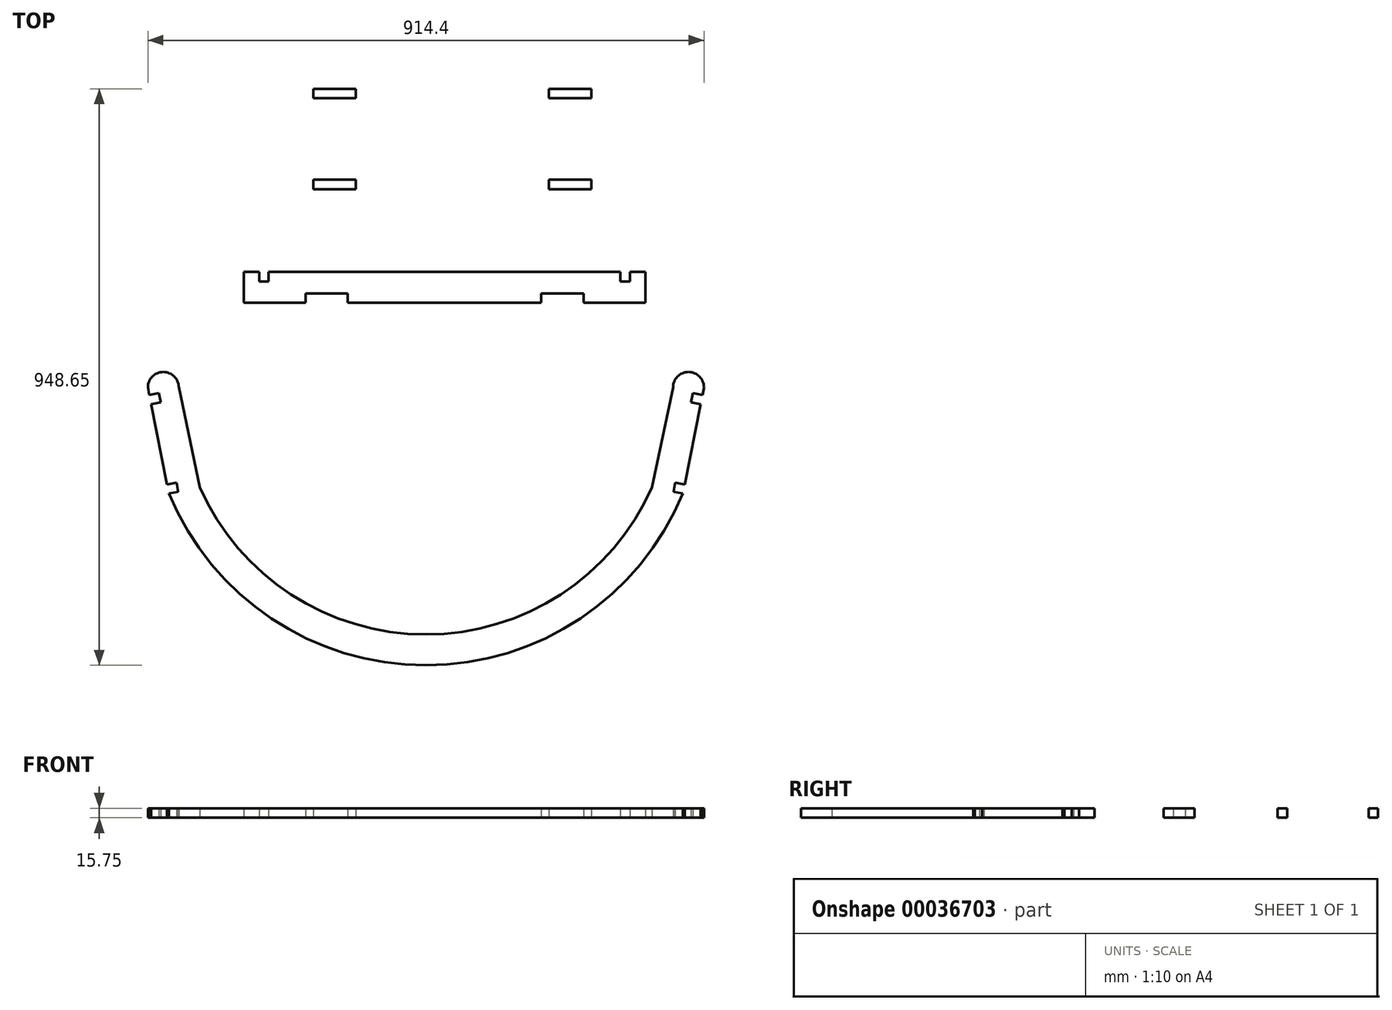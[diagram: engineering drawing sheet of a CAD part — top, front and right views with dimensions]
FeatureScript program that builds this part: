
annotation { "Feature Type Name" : "Feature", "Feature Type Description" : "" }
export const myFeature = defineFeature(function(context is Context, id is Id, definition is map)
    precondition{}
    {
        {
            var Q0;
            Q0=qCreatedBy(makeId("Top.planeOp"),FACE);
            var sketch = newSketch(context, id + "F0", { "sketchPlane" : qUnion([Q0])});
            skArc(sketch, "E0", {"start": v(-422.59, -174.5) * mm, "mid": v(0, -457.2) * mm, "end": v(422.59, -174.5) * mm});
            skArc(sketch, "E1.0", {"start": v(-371.66, -164.4) * mm, "mid": v(0, -406.4) * mm, "end": v(371.66, -164.4) * mm});
            skArc(sketch, "E2", {"start": v(-406.4, 0) * mm, "mid": v(-431.8, 25.4) * mm, "end": v(-457.2, 0) * mm});
            skArc(sketch, "E3", {"start": v(457.2, 0) * mm, "mid": v(431.8, 25.4) * mm, "end": v(406.4, 0) * mm});
            skLineSegment(sketch, "E4", {"start": v(-457.2, 0) * mm, "end": v(-422.59, -174.5) * mm});
            skLineSegment(sketch, "E5", {"start": v(-406.4, 0) * mm, "end": v(-371.66, -164.4) * mm});
            skPoint(sketch, "E6.endSnap0", {"position": v(0, -406.4) * mm});
            skLineSegment(sketch, "E7.MirrorCS", {"start": v(406.4, 0) * mm, "end": v(371.66, -164.4) * mm});
            skLineSegment(sketch, "E8.MirrorCS", {"start": v(457.2, 0) * mm, "end": v(422.59, -174.5) * mm});
            skLineSegment(sketch, "E9.MirrorCS", {"start": v(454.7, -12.56) * mm, "end": v(451.73, -27.57) * mm});
            skLineSegment(sketch, "E10.MirrorCS", {"start": v(439.3, -9.3) * mm, "end": v(454.7, -12.56) * mm});
            skLineSegment(sketch, "E11.MirrorCS", {"start": v(407.1, -171.64) * mm, "end": v(422.59, -174.5) * mm});
            skLineSegment(sketch, "E12.MirrorCS", {"start": v(425.56, -159.5) * mm, "end": v(409.93, -156.4) * mm});
            skLineSegment(sketch, "E13.MirrorCS", {"start": v(409.93, -156.4) * mm, "end": v(407.1, -171.64) * mm});
            skLineSegment(sketch, "E14.MirrorCS", {"start": v(451.73, -27.57) * mm, "end": v(436.1, -24.47) * mm});
            skLineSegment(sketch, "E15.MirrorCS", {"start": v(439.3, -9.3) * mm, "end": v(436.1, -24.47) * mm});
            skLineSegment(sketch, "E16.bottom", {"start": v(-299.66, 189.87) * mm, "end": v(360.74, 189.87) * mm});
            skLineSegment(sketch, "E16.top", {"start": v(-299.66, 139.07) * mm, "end": v(360.74, 139.07) * mm});
            skLineSegment(sketch, "E16.left", {"start": v(-299.66, 189.87) * mm, "end": v(-299.66, 139.07) * mm});
            skLineSegment(sketch, "E16.right", {"start": v(360.74, 189.87) * mm, "end": v(360.74, 139.07) * mm});
            skLineSegment(sketch, "E17.right", {"start": v(-274.26, 189.87) * mm, "end": v(-274.26, 174.12) * mm});
            skLineSegment(sketch, "E18.bottom", {"start": v(-274.26, 174.12) * mm, "end": v(-258.51, 174.12) * mm});
            skLineSegment(sketch, "E18.top", {"start": v(-283.91, 189.87) * mm, "end": v(-258.51, 189.87) * mm});
            skLineSegment(sketch, "E18.right", {"start": v(-258.51, 174.12) * mm, "end": v(-258.51, 189.87) * mm});
            skLineSegment(sketch, "E19.bottom", {"start": v(-198.06, 154.82) * mm, "end": v(-128.28, 154.82) * mm});
            skLineSegment(sketch, "E19.top", {"start": v(-198.06, 139.07) * mm, "end": v(-128.28, 139.07) * mm});
            skLineSegment(sketch, "E19.left", {"start": v(-198.06, 154.82) * mm, "end": v(-198.06, 139.07) * mm});
            skLineSegment(sketch, "E19.right", {"start": v(-128.28, 154.82) * mm, "end": v(-128.28, 139.07) * mm});
            skPoint(sketch, "E20", {"position": v(-198.06, 139.07) * mm});
            skLineSegment(sketch, "E21.MirrorCS", {"start": v(319.6, 174.12) * mm, "end": v(319.6, 189.87) * mm});
            skLineSegment(sketch, "E22.MirrorCS", {"start": v(335.34, 189.87) * mm, "end": v(335.34, 174.12) * mm});
            skLineSegment(sketch, "E23.MirrorCS", {"start": v(259.14, 154.82) * mm, "end": v(259.14, 139.07) * mm});
            skPoint(sketch, "E24.MirrorP", {"position": v(259.14, 139.07) * mm});
            skLineSegment(sketch, "E25.MirrorCS", {"start": v(259.14, 139.07) * mm, "end": v(189.36, 139.07) * mm});
            skLineSegment(sketch, "E26.MirrorCS", {"start": v(335.34, 174.12) * mm, "end": v(319.6, 174.12) * mm});
            skLineSegment(sketch, "E27.MirrorCS", {"start": v(259.14, 154.82) * mm, "end": v(189.36, 154.82) * mm});
            skLineSegment(sketch, "E28.MirrorCS", {"start": v(189.36, 154.82) * mm, "end": v(189.36, 139.07) * mm});
            skPoint(sketch, "E29.MirrorP", {"position": v(272.17, 475.7) * mm});
            skLineSegment(sketch, "E30.bottom", {"start": v(-185.03, 491.45) * mm, "end": v(-115.25, 491.45) * mm});
            skPoint(sketch, "E31", {"position": v(-185.03, 475.7) * mm});
            skLineSegment(sketch, "E32.top", {"start": v(-286.63, 475.7) * mm, "end": v(373.77, 475.7) * mm});
            skLineSegment(sketch, "E33.MirrorCS", {"start": v(272.17, 491.45) * mm, "end": v(202.4, 491.45) * mm});
            skLineSegment(sketch, "E30.top", {"start": v(-185.03, 475.7) * mm, "end": v(-115.25, 475.7) * mm});
            skLineSegment(sketch, "E34.MirrorCS", {"start": v(272.17, 475.7) * mm, "end": v(202.4, 475.7) * mm});
            skLineSegment(sketch, "E35.MirrorCS", {"start": v(202.4, 491.45) * mm, "end": v(202.4, 475.7) * mm});
            skLineSegment(sketch, "E30.right", {"start": v(-115.25, 491.45) * mm, "end": v(-115.25, 475.7) * mm});
            skLineSegment(sketch, "E36.MirrorCS", {"start": v(272.17, 491.45) * mm, "end": v(272.17, 475.7) * mm});
            skLineSegment(sketch, "E30.left", {"start": v(-185.03, 491.45) * mm, "end": v(-185.03, 475.7) * mm});
            skLineSegment(sketch, "E37", {"start": v(0, -406.4) * mm, "end": v(0, 93.54) * mm});
            skLineSegment(sketch, "E38.right", {"start": v(373.77, 475.7) * mm, "end": v(373.77, 342.1) * mm});
            skLineSegment(sketch, "E39.MirrorCS", {"start": v(-115.25, 326.35) * mm, "end": v(-115.25, 342.1) * mm});
            skLineSegment(sketch, "E40.MirrorCS", {"start": v(-185.03, 326.35) * mm, "end": v(-185.03, 342.1) * mm});
            skLineSegment(sketch, "E41.MirrorCS", {"start": v(272.17, 326.35) * mm, "end": v(272.17, 342.1) * mm});
            skLineSegment(sketch, "E42.MirrorCS", {"start": v(202.4, 326.35) * mm, "end": v(202.4, 342.1) * mm});
            skPoint(sketch, "E43.MirrorP", {"position": v(-185.03, 342.1) * mm});
            skLineSegment(sketch, "E44.MirrorCS", {"start": v(272.17, 326.35) * mm, "end": v(202.4, 326.35) * mm});
            skLineSegment(sketch, "E45.MirrorCS", {"start": v(-185.03, 326.35) * mm, "end": v(-115.25, 326.35) * mm});
            skLineSegment(sketch, "E46.MirrorCS", {"start": v(272.17, 342.1) * mm, "end": v(202.4, 342.1) * mm});
            skPoint(sketch, "E47.MirrorP", {"position": v(272.17, 342.1) * mm});
            skLineSegment(sketch, "E48.MirrorCS", {"start": v(-185.03, 342.1) * mm, "end": v(-115.25, 342.1) * mm});
            skLineSegment(sketch, "E49", {"start": v(-286.63, 475.7) * mm, "end": v(-286.63, 342.1) * mm});
            skLineSegment(sketch, "E50", {"start": v(-286.63, 342.1) * mm, "end": v(373.77, 342.1) * mm});
            skPoint(sketch, "E51", {"position": v(451.73, -27.57) * mm});
            skLineSegment(sketch, "E52.MirrorCS", {"start": v(-451.73, -27.57) * mm, "end": v(-436.1, -24.47) * mm});
            skLineSegment(sketch, "E53.MirrorCS", {"start": v(-439.3, -9.3) * mm, "end": v(-436.1, -24.47) * mm});
            skLineSegment(sketch, "E54.MirrorCS", {"start": v(-439.3, -9.3) * mm, "end": v(-454.7, -12.56) * mm});
            skLineSegment(sketch, "E55.MirrorCS", {"start": v(-454.7, -12.56) * mm, "end": v(-451.73, -27.57) * mm});
            skLineSegment(sketch, "E56.MirrorCS", {"start": v(-409.93, -156.4) * mm, "end": v(-407.1, -171.64) * mm});
            skLineSegment(sketch, "E57.MirrorCS", {"start": v(-407.1, -171.64) * mm, "end": v(-422.59, -174.5) * mm});
            skLineSegment(sketch, "E58.MirrorCS", {"start": v(-425.56, -159.5) * mm, "end": v(-409.93, -156.4) * mm});
            skPoint(sketch, "E59.MirrorP", {"position": v(-451.73, -27.57) * mm});
            skSolve(sketch);
        }
        {
            var Q0;
            {var subQ8=sQuery(id+"F0.wireOp",EDGE,"E30.top");Q0=makeQuery(id+"F0.imprint","IMPRINT",FACE,{"disambiguationData":[TD([[makeQuery(id+"F0.imprint","IMPRINT",EDGE,{"derivedFrom":subQ8}),-1.0]])]});}
            var Q1;
            Q1=makeQuery(id+"F0.imprint","IMPRINT",FACE,{"disambiguationData":[TD([[makeQuery(id+"F0.imprint","IMPRINT",EDGE,{"derivedFrom":sQuery(id+"F0.wireOp",EDGE,"E30.bottom")}),-1.0]])]});
            var Q2;
            {var subQ2=sQuery(id+"F0.wireOp",EDGE,"E39.MirrorCS");Q2=makeQuery(id+"F0.imprint","IMPRINT",FACE,{"disambiguationData":[TD([[makeQuery(id+"F0.imprint","IMPRINT",EDGE,{"derivedFrom":subQ2}),1.0]])]});}
            var Q3;
            Q3=makeQuery(id+"F0.imprint","IMPRINT",FACE,{"disambiguationData":[TD([[makeQuery(id+"F0.imprint","IMPRINT",EDGE,{"derivedFrom":sQuery(id+"F0.wireOp",EDGE,"E33.MirrorCS")}),1.0]])]});
            var Q4;
            {var subQ2=sQuery(id+"F0.wireOp",EDGE,"E41.MirrorCS");Q4=makeQuery(id+"F0.imprint","IMPRINT",FACE,{"disambiguationData":[TD([[makeQuery(id+"F0.imprint","IMPRINT",EDGE,{"derivedFrom":subQ2}),1.0]])]});}
            var Q5;
            {var subQ10=sQuery(id+"F0.wireOp",EDGE,"E16.left");Q5=makeQuery(id+"F0.imprint","IMPRINT",FACE,{"disambiguationData":[TD([[makeQuery(id+"F0.imprint","IMPRINT",EDGE,{"derivedFrom":subQ10}),1.0]])]});}
            var Q6;
            Q6=makeQuery(id+"F0.imprint","IMPRINT",FACE,{"disambiguationData":[TD([[makeQuery(id+"F0.imprint","IMPRINT",EDGE,{"derivedFrom":sQuery(id+"F0.wireOp",EDGE,"E0")}),1.0]])]});
            extrude(context, id + "F1", {"entities" : qUnion([Q0, Q1, Q2, Q3, Q4, Q5, Q6]), "depth" : 15.75 * mm});
        }
    });
